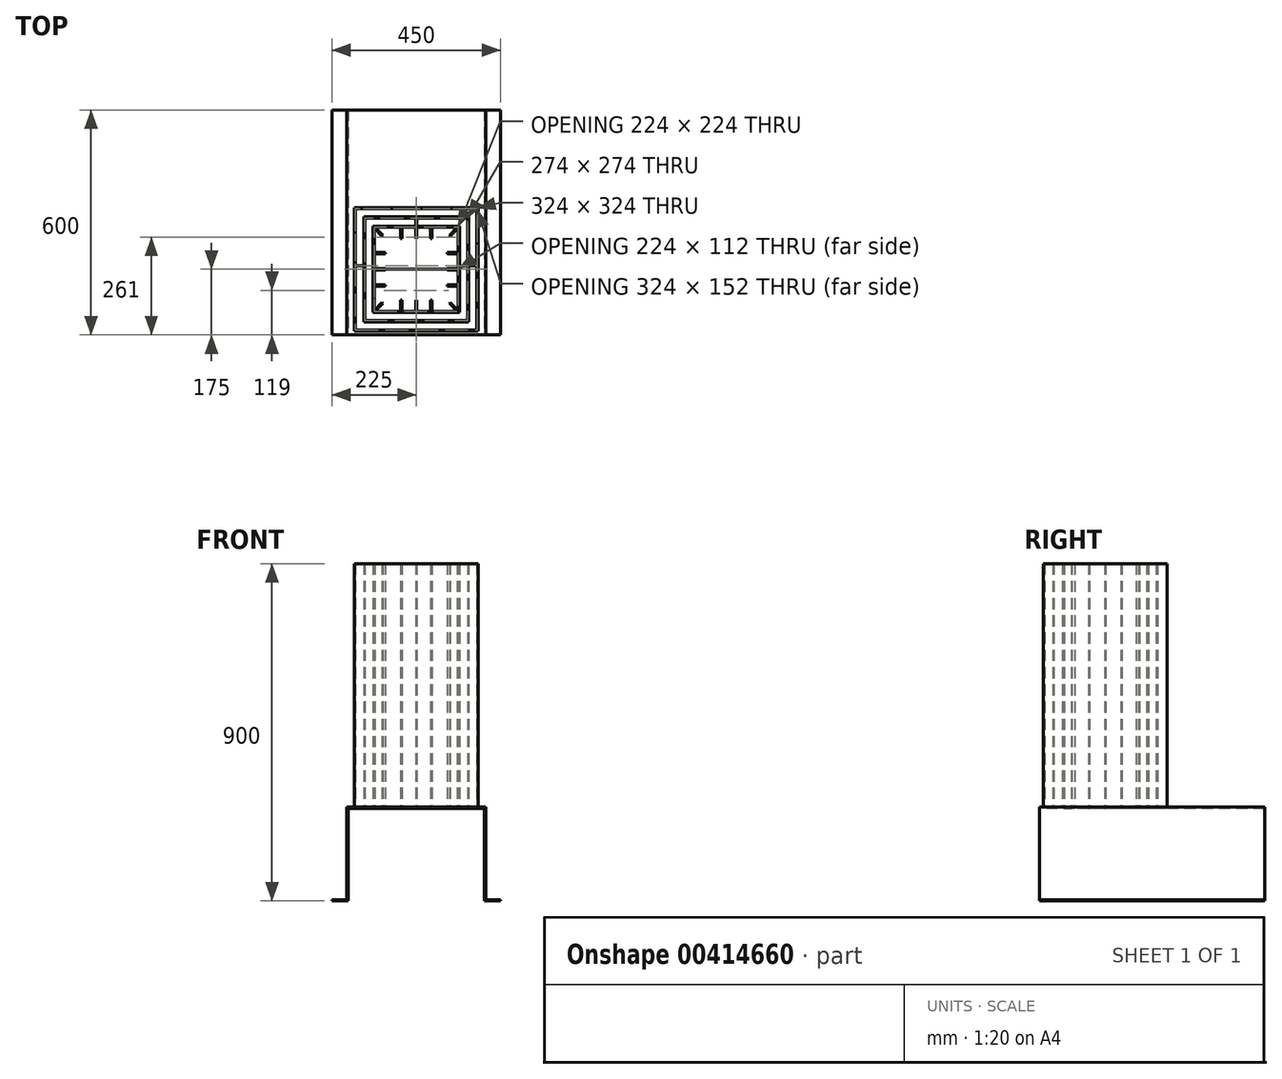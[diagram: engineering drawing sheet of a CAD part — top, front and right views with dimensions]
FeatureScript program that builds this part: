
annotation { "Feature Type Name" : "Feature", "Feature Type Description" : "" }
export const myFeature = defineFeature(function(context is Context, id is Id, definition is map)
    precondition{}
    {
        {
            assignVariable(context, id + "F0", {"name" : "M", "anyValue" : 600});
        }
        {
            assignVariable(context, id + "F1", {"name" : "Y", "anyValue" : 900});
        }
        {
            var Q0;
            Q0=qCreatedBy(makeId("Front.planeOp"),FACE);
            var sketch = newSketch(context, id + "F2", { "sketchPlane" : qUnion([Q0])});
            skLineSegment(sketch, "E0", {"start": v(-182, 0) * mm, "end": v(182, 0) * mm});
            skLineSegment(sketch, "E1", {"start": v(182, 0) * mm, "end": v(182, -247) * mm});
            skLineSegment(sketch, "E2", {"start": v(-182, 0) * mm, "end": v(-182, -247) * mm});
            skLineSegment(sketch, "E3", {"start": v(-182, -247) * mm, "end": v(-225, -247) * mm});
            skLineSegment(sketch, "E4", {"start": v(182, -247) * mm, "end": v(225, -247) * mm});
            skLineSegment(sketch, "E5.0", {"start": v(-185, -244) * mm, "end": v(-225, -244) * mm});
            skLineSegment(sketch, "E5.1", {"start": v(185, -244) * mm, "end": v(225, -244) * mm});
            skLineSegment(sketch, "E5.2", {"start": v(185, 3) * mm, "end": v(185, -244) * mm});
            skLineSegment(sketch, "E5.3", {"start": v(-185, 3) * mm, "end": v(185, 3) * mm});
            skLineSegment(sketch, "E5.4", {"start": v(-185, 3) * mm, "end": v(-185, -244) * mm});
            skLineSegment(sketch, "E6", {"start": v(-225, -244) * mm, "end": v(-225, -247) * mm});
            skLineSegment(sketch, "E7", {"start": v(225, -244) * mm, "end": v(225, -247) * mm});
            skSolve(sketch);
        }
        {
            var Q0;
            Q0=makeQuery(id+"F2.imprint","IMPRINT",FACE,{"disambiguationData":[TD([[makeQuery(id+"F2.imprint","IMPRINT",EDGE,{"derivedFrom":sQuery(id+"F2.wireOp",EDGE,"E0")}),1.0]])]});
            extrude(context, id + "F3", {"entities" : qUnion([Q0]), "oppositeDirection" : true, "depth" : (getVariable(context, 'M')) * mm});
        }
        {
            var Q0;
            Q0=makeQuery(id+"F3.opExtrude","SWEPT_FACE",FACE,{"disambiguationData":[OSD([sQuery(id+"F2.wireOp",EDGE,"E5.3")])]});
            var sketch = newSketch(context, id + "F4", { "sketchPlane" : qUnion([Q0])});
            skLineSegment(sketch, "E8.0.0", {"start": v(-185, 0) * mm, "end": v(185, 0) * mm});
            skLineSegment(sketch, "E8.0.1", {"start": v(185, 0) * mm, "end": v(185, 600) * mm});
            skLineSegment(sketch, "E8.0.2", {"start": v(185, 600) * mm, "end": v(-185, 600) * mm});
            skLineSegment(sketch, "E8.0.3", {"start": v(-185, 600) * mm, "end": v(-185, 0) * mm});
            skLineSegment(sketch, "E9", {"start": v(0, 0) * mm, "end": v(0, 600) * mm, "construction": true});
            skLineSegment(sketch, "E10.bottom", {"start": v(165, 10) * mm, "end": v(-165, 10) * mm});
            skLineSegment(sketch, "E10.top", {"start": v(165, 340) * mm, "end": v(-165, 340) * mm});
            skLineSegment(sketch, "E10.left", {"start": v(165, 10) * mm, "end": v(165, 340) * mm});
            skLineSegment(sketch, "E10.right", {"start": v(-165, 10) * mm, "end": v(-165, 340) * mm});
            skPoint(sketch, "E10.middle", {"position": v(0, 175) * mm});
            skLineSegment(sketch, "E11.bottom", {"start": v(140, 35) * mm, "end": v(-140, 35) * mm});
            skLineSegment(sketch, "E11.top", {"start": v(140, 315) * mm, "end": v(-140, 315) * mm});
            skLineSegment(sketch, "E11.left", {"start": v(140, 35) * mm, "end": v(140, 315) * mm});
            skLineSegment(sketch, "E11.right", {"start": v(-140, 35) * mm, "end": v(-140, 315) * mm});
            skLineSegment(sketch, "E12.bottom", {"start": v(115, 60) * mm, "end": v(-115, 60) * mm});
            skLineSegment(sketch, "E12.top", {"start": v(115, 290) * mm, "end": v(1.5, 290) * mm});
            skLineSegment(sketch, "E12.left", {"start": v(115, 60) * mm, "end": v(115, 290) * mm});
            skLineSegment(sketch, "E12.right", {"start": v(-115, 60) * mm, "end": v(-115, 290) * mm});
            skLineSegment(sketch, "E13.0", {"start": v(162, 337) * mm, "end": v(-162, 337) * mm});
            skLineSegment(sketch, "E13.1", {"start": v(162, 13) * mm, "end": v(162, 337) * mm});
            skLineSegment(sketch, "E13.2", {"start": v(162, 13) * mm, "end": v(-162, 13) * mm});
            skLineSegment(sketch, "E13.3", {"start": v(-162, 13) * mm, "end": v(-162, 337) * mm});
            skLineSegment(sketch, "E14.0", {"start": v(137, 312) * mm, "end": v(-137, 312) * mm});
            skLineSegment(sketch, "E14.1", {"start": v(137, 38) * mm, "end": v(137, 312) * mm});
            skLineSegment(sketch, "E14.2", {"start": v(137, 38) * mm, "end": v(-137, 38) * mm});
            skLineSegment(sketch, "E14.3", {"start": v(-137, 38) * mm, "end": v(-137, 312) * mm});
            skLineSegment(sketch, "E15.1", {"start": v(112, 65.12) * mm, "end": v(112, 130.5) * mm});
            skLineSegment(sketch, "E15.3", {"start": v(-112, 65.12) * mm, "end": v(-112, 130.5) * mm});
            skLineSegment(sketch, "E16", {"start": v(-82, 175) * mm, "end": v(82, 175) * mm});
            skLineSegment(sketch, "E17", {"start": v(-162, 185) * mm, "end": v(-140, 185) * mm});
            skLineSegment(sketch, "E18", {"start": v(140, 185) * mm, "end": v(162, 185) * mm});
            skLineSegment(sketch, "E19.top", {"start": v(-1.5, 257) * mm, "end": v(1.5, 257) * mm});
            skLineSegment(sketch, "E19.left", {"start": v(-1.5, 287) * mm, "end": v(-1.5, 257) * mm});
            skLineSegment(sketch, "E19.right", {"start": v(1.5, 287) * mm, "end": v(1.5, 257) * mm});
            skPoint(sketch, "E19.middle", {"position": v(0, 272) * mm});
            skLineSegment(sketch, "E20.1.0.0", {"start": v(38.5, 287) * mm, "end": v(38.5, 257) * mm});
            skLineSegment(sketch, "E20.1.0.1", {"start": v(41.5, 287) * mm, "end": v(41.5, 257) * mm});
            skLineSegment(sketch, "E20.1.0.2", {"start": v(38.5, 257) * mm, "end": v(41.5, 257) * mm});
            skLineSegment(sketch, "E20.direction1", {"start": v(-1.5, 257) * mm, "end": v(38.5, 257) * mm, "construction": true});
            skLineSegment(sketch, "E21.MirrorCS", {"start": v(-38.5, 287) * mm, "end": v(-38.5, 257) * mm});
            skLineSegment(sketch, "E22.MirrorCS", {"start": v(-41.5, 287) * mm, "end": v(-41.5, 257) * mm});
            skLineSegment(sketch, "E23.MirrorCS", {"start": v(1.5, 257) * mm, "end": v(-38.5, 257) * mm, "construction": true});
            skLineSegment(sketch, "E24.MirrorCS", {"start": v(-38.5, 257) * mm, "end": v(-41.5, 257) * mm});
            skLineSegment(sketch, "E25.MirrorCS", {"start": v(-38.5, 93) * mm, "end": v(-41.5, 93) * mm});
            skLineSegment(sketch, "E26.MirrorCS", {"start": v(38.5, 93) * mm, "end": v(41.5, 93) * mm});
            skLineSegment(sketch, "E27.MirrorCS", {"start": v(-1.5, 93) * mm, "end": v(1.5, 93) * mm});
            skLineSegment(sketch, "E28.MirrorCS", {"start": v(-38.5, 63) * mm, "end": v(-38.5, 93) * mm});
            skLineSegment(sketch, "E29.MirrorCS", {"start": v(-1.5, 63) * mm, "end": v(-1.5, 93) * mm});
            skLineSegment(sketch, "E30.MirrorCS", {"start": v(1.5, 93) * mm, "end": v(-38.5, 93) * mm, "construction": true});
            skLineSegment(sketch, "E31.MirrorCS", {"start": v(-1.5, 93) * mm, "end": v(38.5, 93) * mm, "construction": true});
            skLineSegment(sketch, "E32.MirrorCS", {"start": v(1.5, 63) * mm, "end": v(1.5, 93) * mm});
            skLineSegment(sketch, "E33.MirrorCS", {"start": v(41.5, 63) * mm, "end": v(41.5, 93) * mm});
            skLineSegment(sketch, "E34.MirrorCS", {"start": v(38.5, 63) * mm, "end": v(38.5, 93) * mm});
            skLineSegment(sketch, "E35.MirrorCS", {"start": v(0, 350) * mm, "end": v(0, -250) * mm, "construction": true});
            skPoint(sketch, "E36.MirrorP", {"position": v(0, 78) * mm});
            skLineSegment(sketch, "E37.MirrorCS", {"start": v(-41.5, 63) * mm, "end": v(-41.5, 93) * mm});
            skLineSegment(sketch, "E38.bottom", {"start": v(112, 176.5) * mm, "end": v(82, 176.5) * mm});
            skLineSegment(sketch, "E38.top", {"start": v(112, 173.5) * mm, "end": v(82, 173.5) * mm});
            skLineSegment(sketch, "E38.right", {"start": v(82, 176.5) * mm, "end": v(82, 173.5) * mm});
            skLineSegment(sketch, "E39", {"start": v(112, 196.5) * mm, "end": v(57.33, 196.5) * mm, "construction": true});
            skLineSegment(sketch, "E40.MirrorCS", {"start": v(112, 216.5) * mm, "end": v(82, 216.5) * mm});
            skLineSegment(sketch, "E41.MirrorCS", {"start": v(82, 216.5) * mm, "end": v(82, 219.5) * mm});
            skLineSegment(sketch, "E42.MirrorCS", {"start": v(112, 219.5) * mm, "end": v(82, 219.5) * mm});
            skLineSegment(sketch, "E43.MirrorCS", {"start": v(112, 133.5) * mm, "end": v(82, 133.5) * mm});
            skLineSegment(sketch, "E44.MirrorCS", {"start": v(112, 130.5) * mm, "end": v(82, 130.5) * mm});
            skLineSegment(sketch, "E45.MirrorCS", {"start": v(82, 133.5) * mm, "end": v(82, 130.5) * mm});
            skLineSegment(sketch, "E46.MirrorCS", {"start": v(-82, 133.5) * mm, "end": v(-82, 130.5) * mm});
            skLineSegment(sketch, "E47.MirrorCS", {"start": v(-82, 176.5) * mm, "end": v(-82, 173.5) * mm});
            skLineSegment(sketch, "E48.MirrorCS", {"start": v(-82, 216.5) * mm, "end": v(-82, 219.5) * mm});
            skLineSegment(sketch, "E49.MirrorCS", {"start": v(-112, 130.5) * mm, "end": v(-82, 130.5) * mm});
            skLineSegment(sketch, "E50.MirrorCS", {"start": v(-112, 133.5) * mm, "end": v(-82, 133.5) * mm});
            skLineSegment(sketch, "E51.MirrorCS", {"start": v(-112, 173.5) * mm, "end": v(-82, 173.5) * mm});
            skLineSegment(sketch, "E52.MirrorCS", {"start": v(-112, 176.5) * mm, "end": v(-82, 176.5) * mm});
            skLineSegment(sketch, "E53.MirrorCS", {"start": v(-112, 216.5) * mm, "end": v(-82, 216.5) * mm});
            skLineSegment(sketch, "E54.MirrorCS", {"start": v(-112, 219.5) * mm, "end": v(-82, 219.5) * mm});
            skLineSegment(sketch, "E55.trimOffspring", {"start": v(-41.5, 287) * mm, "end": v(-109.88, 287) * mm});
            skLineSegment(sketch, "E56.trimOffspring", {"start": v(-1.5, 287) * mm, "end": v(-38.5, 287) * mm});
            skLineSegment(sketch, "E57.trimOffspring", {"start": v(38.5, 287) * mm, "end": v(1.5, 287) * mm});
            skLineSegment(sketch, "E58.trimOffspring", {"start": v(109.88, 287) * mm, "end": v(41.5, 287) * mm});
            skLineSegment(sketch, "E59.trimOffspring", {"start": v(112, 176.5) * mm, "end": v(112, 216.5) * mm});
            skLineSegment(sketch, "E60.trimOffspring", {"start": v(112, 219.5) * mm, "end": v(112, 284.88) * mm});
            skLineSegment(sketch, "E61.trimOffspring", {"start": v(112, 133.5) * mm, "end": v(112, 173.5) * mm});
            skLineSegment(sketch, "E62.trimOffspring", {"start": v(109.88, 63) * mm, "end": v(41.5, 63) * mm});
            skLineSegment(sketch, "E63.trimOffspring", {"start": v(38.5, 63) * mm, "end": v(1.5, 63) * mm});
            skLineSegment(sketch, "E64.trimOffspring", {"start": v(-1.5, 63) * mm, "end": v(-38.5, 63) * mm});
            skLineSegment(sketch, "E65.trimOffspring", {"start": v(-41.5, 63) * mm, "end": v(-109.88, 63) * mm});
            skLineSegment(sketch, "E66.trimOffspring", {"start": v(-112, 133.5) * mm, "end": v(-112, 173.5) * mm});
            skLineSegment(sketch, "E67.trimOffspring", {"start": v(-112, 176.5) * mm, "end": v(-112, 216.5) * mm});
            skLineSegment(sketch, "E68.trimOffspring", {"start": v(-112, 219.5) * mm, "end": v(-112, 284.88) * mm});
            skLineSegment(sketch, "E69", {"start": v(-109.88, 287) * mm, "end": v(-88.67, 265.79) * mm});
            skLineSegment(sketch, "E70", {"start": v(-88.67, 265.79) * mm, "end": v(-90.79, 263.67) * mm});
            skLineSegment(sketch, "E71", {"start": v(-90.79, 263.67) * mm, "end": v(-112, 284.88) * mm});
            skPoint(sketch, "E72.orphan", {"position": v(-112, 287) * mm});
            skLineSegment(sketch, "E73", {"start": v(-115, 290) * mm, "end": v(-112, 287) * mm, "construction": true});
            skLineSegment(sketch, "E74.MirrorCS", {"start": v(109.88, 287) * mm, "end": v(88.67, 265.79) * mm});
            skLineSegment(sketch, "E75.MirrorCS", {"start": v(90.79, 263.67) * mm, "end": v(112, 284.88) * mm});
            skLineSegment(sketch, "E76.MirrorCS", {"start": v(88.67, 265.79) * mm, "end": v(90.79, 263.67) * mm});
            skLineSegment(sketch, "E77.MirrorCS", {"start": v(-109.88, 63) * mm, "end": v(-88.67, 84.21) * mm});
            skLineSegment(sketch, "E78.MirrorCS", {"start": v(-90.79, 86.33) * mm, "end": v(-112, 65.12) * mm});
            skLineSegment(sketch, "E79.MirrorCS", {"start": v(-88.67, 84.21) * mm, "end": v(-90.79, 86.33) * mm});
            skLineSegment(sketch, "E80.MirrorCS", {"start": v(109.88, 63) * mm, "end": v(88.67, 84.21) * mm});
            skLineSegment(sketch, "E81.MirrorCS", {"start": v(90.79, 86.33) * mm, "end": v(112, 65.12) * mm});
            skLineSegment(sketch, "E82.MirrorCS", {"start": v(88.67, 84.21) * mm, "end": v(90.79, 86.33) * mm});
            skPoint(sketch, "E83.orphan", {"position": v(112, 287) * mm});
            skPoint(sketch, "E84.orphan", {"position": v(112, 63) * mm});
            skPoint(sketch, "E85.orphan", {"position": v(-112, 63) * mm});
            skLineSegment(sketch, "E86", {"start": v(-1.5, 290) * mm, "end": v(-1.5, 310) * mm});
            skLineSegment(sketch, "E87", {"start": v(-1.5, 310) * mm, "end": v(1.5, 310) * mm});
            skLineSegment(sketch, "E88", {"start": v(1.5, 310) * mm, "end": v(1.5, 290) * mm});
            skLineSegment(sketch, "E89.trimOffspring", {"start": v(-1.5, 290) * mm, "end": v(-115, 290) * mm});
            skSolve(sketch);
        }
        {
            var Q0;
            {var subQ2=sQuery(id+"F4.wireOp",EDGE,"E11.top");Q0=makeQuery(id+"F4.imprint","IMPRINT",FACE,{"disambiguationData":[TD([[makeQuery(id+"F4.imprint","IMPRINT",EDGE,{"derivedFrom":subQ2}),-1.0]])]});}
            var Q1;
            Q1=makeQuery(id+"F4.imprint","IMPRINT",FACE,{"disambiguationData":[TD([[makeQuery(id+"F4.imprint","IMPRINT",EDGE,{"derivedFrom":sQuery(id+"F4.wireOp",EDGE,"E15.1")}),1.0]])]});
            extrude(context, id + "F5", {"entities" : qUnion([Q0, Q1]), "operationType" : NewBodyOperationType.REMOVE, "endBound" : BoundingType.THROUGH_ALL, "oppositeDirection" : true, "depth" : 25 * mm});
        }
        {
            var Q0;
            Q0=makeQuery(id+"F4.imprint","IMPRINT",FACE,{"disambiguationData":[TD([[makeQuery(id+"F4.imprint","IMPRINT",EDGE,{"derivedFrom":sQuery(id+"F4.wireOp",EDGE,"E12.bottom")}),-1.0]])]});
            extrude(context, id + "F6", {"entities" : qUnion([Q0]), "depth" : ((getVariable(context, 'Y')) - 250) * mm});
        }
        {
            var Q0;
            {var subQ3=sQuery(id+"F4.wireOp",EDGE,"E11.bottom");Q0=makeQuery(id+"F4.imprint","IMPRINT",FACE,{"disambiguationData":[TD([[makeQuery(id+"F4.imprint","IMPRINT",EDGE,{"derivedFrom":subQ3}),-1.0]])]});}
            extrude(context, id + "F7", {"entities" : qUnion([Q0]), "depth" : (getVariable(context, 'Y') - 250) * mm});
        }
        {
            var Q0;
            Q0=makeQuery(id+"F4.imprint","IMPRINT",FACE,{"disambiguationData":[TD([[makeQuery(id+"F4.imprint","IMPRINT",EDGE,{"derivedFrom":sQuery(id+"F4.wireOp",EDGE,"E10.bottom")}),-1.0]])]});
            extrude(context, id + "F8", {"entities" : qUnion([Q0]), "depth" : (getVariable(context, 'Y') - 250) * mm});
        }
    });
